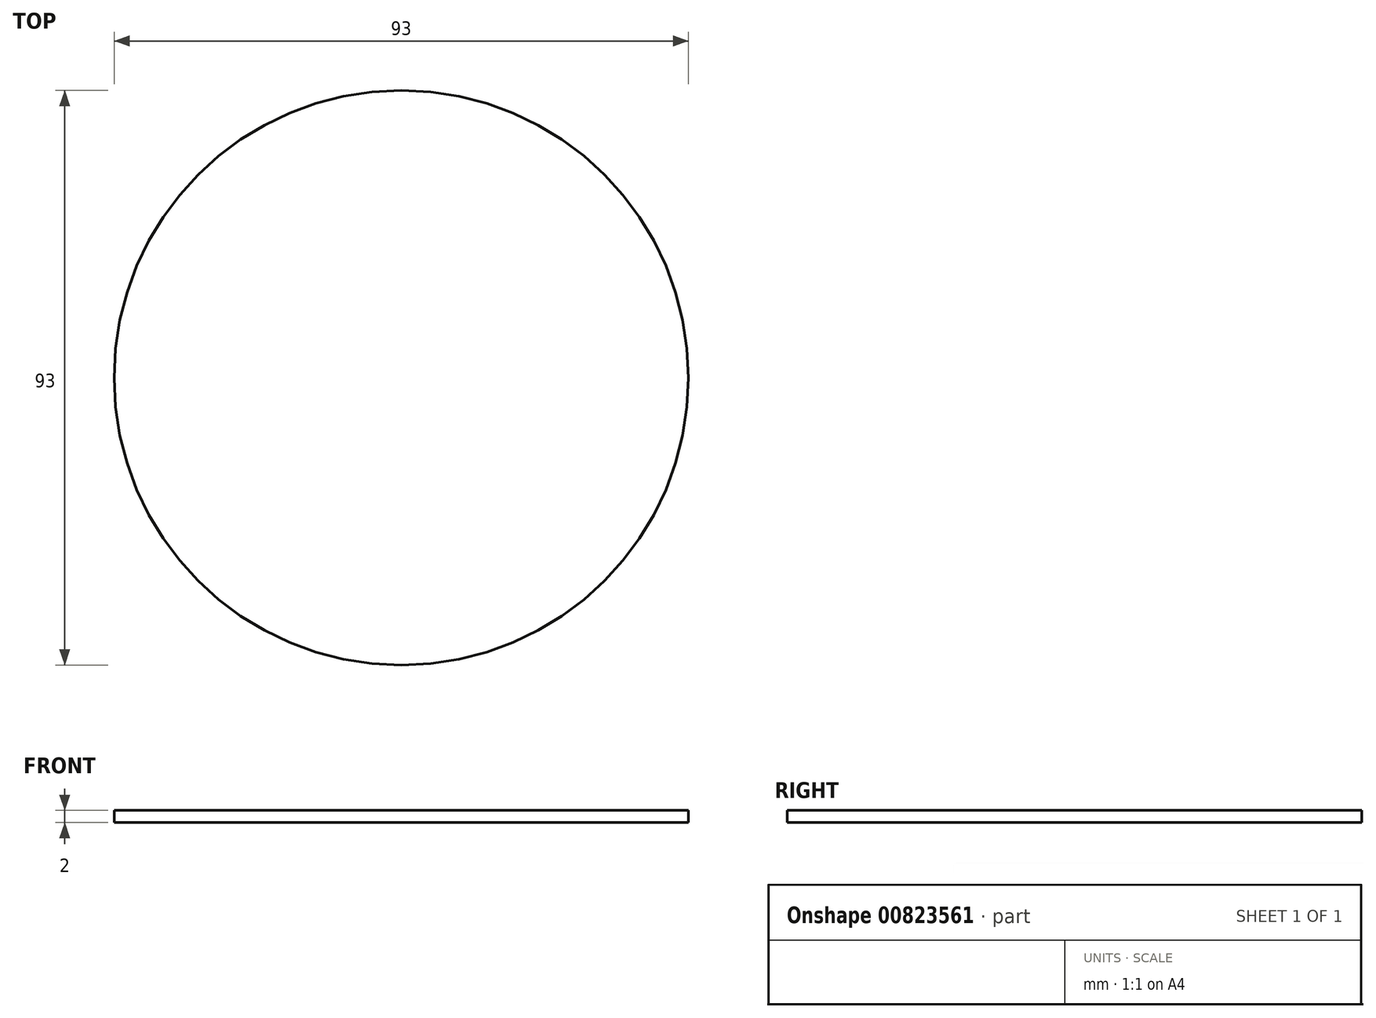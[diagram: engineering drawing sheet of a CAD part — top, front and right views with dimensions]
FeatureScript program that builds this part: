
annotation { "Feature Type Name" : "Feature", "Feature Type Description" : "" }
export const myFeature = defineFeature(function(context is Context, id is Id, definition is map)
    precondition{}
    {
        {
            var Q0;
            Q0=qCreatedBy(makeId("Top.planeOp"),FACE);
            var sketch = newSketch(context, id + "F0", { "sketchPlane" : qUnion([Q0])});
            skCircle(sketch, "E0", {"center": v(0, 0) * mm, "radius": 46.5 * mm});
            skSolve(sketch);
        }
        {
            var Q0;
            Q0 = qSketchRegion(id + "F0", true);
            extrude(context, id + "F1", {"entities" : qUnion([Q0]), "depth" : 2 * mm, "offsetDistance" : 25 * mm});
        }
    });
